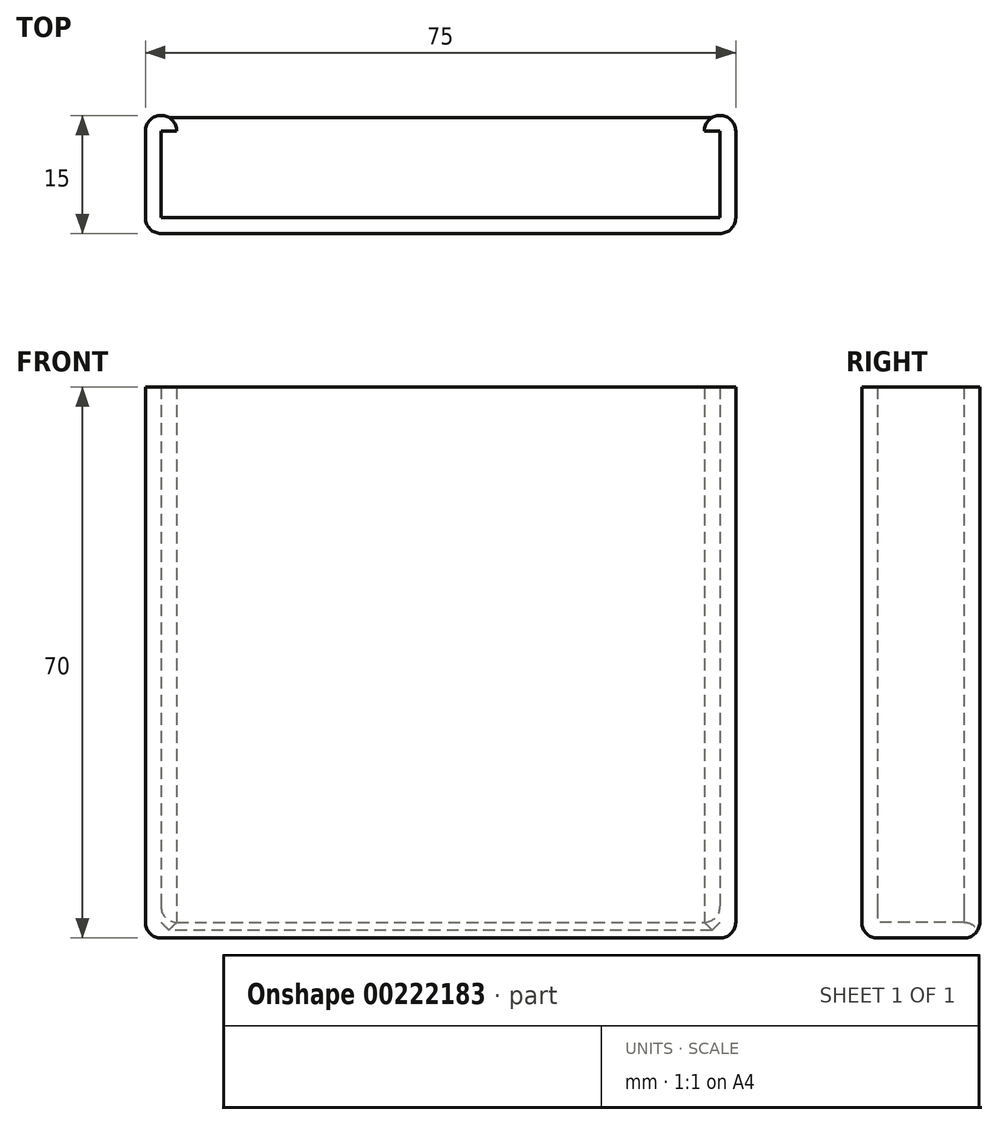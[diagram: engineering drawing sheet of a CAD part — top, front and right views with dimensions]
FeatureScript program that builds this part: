
annotation { "Feature Type Name" : "Feature", "Feature Type Description" : "" }
export const myFeature = defineFeature(function(context is Context, id is Id, definition is map)
    precondition{}
    {
        {
            var Q0;
            Q0=qCreatedBy(makeId("Top.planeOp"),FACE);
            var sketch = newSketch(context, id + "F3", { "sketchPlane" : qUnion([Q0])});
            skLineSegment(sketch, "E0", {"start": v(-37.5, 0) * mm, "end": v(37.5, 0) * mm});
            skLineSegment(sketch, "E1", {"start": v(37.5, 0) * mm, "end": v(37.5, 15) * mm});
            skLineSegment(sketch, "E2", {"start": v(37.5, 15) * mm, "end": v(33.5, 15) * mm});
            skLineSegment(sketch, "E3", {"start": v(33.5, 15) * mm, "end": v(33.5, 13) * mm});
            skLineSegment(sketch, "E4", {"start": v(33.5, 13) * mm, "end": v(35.5, 13) * mm});
            skLineSegment(sketch, "E5", {"start": v(35.5, 13) * mm, "end": v(35.5, 2) * mm});
            skLineSegment(sketch, "E6", {"start": v(35.5, 2) * mm, "end": v(-35.5, 2) * mm});
            skLineSegment(sketch, "E7", {"start": v(-35.5, 2) * mm, "end": v(-35.5, 13) * mm});
            skLineSegment(sketch, "E8", {"start": v(-35.5, 13) * mm, "end": v(-33.5, 13) * mm});
            skLineSegment(sketch, "E9", {"start": v(-33.5, 13) * mm, "end": v(-33.5, 15) * mm});
            skLineSegment(sketch, "E10", {"start": v(-33.5, 15) * mm, "end": v(-37.5, 15) * mm});
            skLineSegment(sketch, "E11", {"start": v(-37.5, 15) * mm, "end": v(-37.5, 0) * mm});
            skSolve(sketch);
        }
        {
            var Q0;
            Q0=qSketchRegion(id+"FxWtbJgkQHIbVw/JA_0",true);
            var Q1;
            Q1=makeQuery(id+"F3.imprint","IMPRINT",FACE,{"disambiguationData":[TD([[makeQuery(id+"F3.imprint","IMPRINT",EDGE,{"derivedFrom":sQuery(id+"F3.wireOp",EDGE,"E0")}),1.0]])]});
            extrude(context, id + "F0", {"entities" : qUnion([Q0, Q1]), "depth" : 70 * mm});
        }
        {
            var Q0;
            Q0=makeQuery(id+"F0.opExtrude","CAP_FACE",FACE,{"disambiguationData":[OSD([sQuery(id+"F3.wireOp",EDGE,"E0"),sQuery(id+"F3.wireOp",EDGE,"E1"),sQuery(id+"F3.wireOp",EDGE,"E2"),sQuery(id+"F3.wireOp",EDGE,"E3"),sQuery(id+"F3.wireOp",EDGE,"E4"),sQuery(id+"F3.wireOp",EDGE,"E5"),sQuery(id+"F3.wireOp",EDGE,"E6"),sQuery(id+"F3.wireOp",EDGE,"E7"),sQuery(id+"F3.wireOp",EDGE,"E8"),sQuery(id+"F3.wireOp",EDGE,"E9"),sQuery(id+"F3.wireOp",EDGE,"E10"),sQuery(id+"F3.wireOp",EDGE,"E11")])],"isStart":true});
            var sketch = newSketch(context, id + "F1", { "sketchPlane" : qUnion([Q0])});
            skLineSegment(sketch, "E12.bottom", {"start": v(37.5, -15) * mm, "end": v(-37.5, -15) * mm});
            skLineSegment(sketch, "E12.top", {"start": v(37.5, 0) * mm, "end": v(-37.5, 0) * mm});
            skLineSegment(sketch, "E12.left", {"start": v(37.5, -15) * mm, "end": v(37.5, 0) * mm});
            skLineSegment(sketch, "E12.right", {"start": v(-37.5, -15) * mm, "end": v(-37.5, 0) * mm});
            skSolve(sketch);
        }
        {
            var Q0;
            Q0=qSketchRegion(id+"F1",true);
            extrude(context, id + "F4", {"entities" : qUnion([Q0]), "operationType" : NewBodyOperationType.ADD, "oppositeDirection" : true, "depth" : 2 * mm});
        }
        {
            var Q0;
            Q0=makeQuery(id+"F0.opExtrude","CAP_EDGE",EDGE,{"disambiguationData":[OSD([sQuery(id+"F3.wireOp",EDGE,"E1")])],"isStart":true});
            var Q1;
            Q1=makeQuery(id+"F0.opExtrude","CAP_EDGE",EDGE,{"disambiguationData":[OSD([sQuery(id+"F3.wireOp",EDGE,"E11")])],"isStart":true});
            var Q2;
            Q2=makeQuery(id+"F4.boolean.opBoolean","INTERSECT",EDGE,{"derivedFrom":[makeQuery(id+"F0.opExtrude","SWEPT_FACE",FACE,{"disambiguationData":[OSD([sQuery(id+"F3.wireOp",EDGE,"E5")])]}),makeQuery(id+"F4.opExtrude","CAP_FACE",FACE,{"disambiguationData":[OSD([sQuery(id+"F1.wireOp",EDGE,"E12.bottom"),sQuery(id+"F1.wireOp",EDGE,"E12.top"),sQuery(id+"F1.wireOp",EDGE,"E12.left"),sQuery(id+"F1.wireOp",EDGE,"E12.right")])],"isStart":false})]});
            var Q3;
            Q3=makeQuery(id+"F4.boolean.opBoolean","INTERSECT",EDGE,{"derivedFrom":[makeQuery(id+"F0.opExtrude","SWEPT_FACE",FACE,{"disambiguationData":[OSD([sQuery(id+"F3.wireOp",EDGE,"E7")])]}),makeQuery(id+"F4.opExtrude","CAP_FACE",FACE,{"disambiguationData":[OSD([sQuery(id+"F1.wireOp",EDGE,"E12.bottom"),sQuery(id+"F1.wireOp",EDGE,"E12.top"),sQuery(id+"F1.wireOp",EDGE,"E12.left"),sQuery(id+"F1.wireOp",EDGE,"E12.right")])],"isStart":false})]});
            var Q4;
            Q4=makeQuery(id+"F0.opExtrude","SWEPT_EDGE",EDGE,{"disambiguationData":[OSD([sQuery(id+"F3.wireOp",EDGE,"E0"),sQuery(id+"F3.wireOp",EDGE,"E11")])]});
            var Q5;
            Q5=makeQuery(id+"F0.opExtrude","SWEPT_EDGE",EDGE,{"disambiguationData":[OSD([sQuery(id+"F3.wireOp",EDGE,"E0"),sQuery(id+"F3.wireOp",EDGE,"E1")])]});
            var Q6;
            Q6=makeQuery(id+"F0.opExtrude","SWEPT_EDGE",EDGE,{"disambiguationData":[OSD([sQuery(id+"F3.wireOp",EDGE,"E10"),sQuery(id+"F3.wireOp",EDGE,"E11")])]});
            var Q7;
            Q7=makeQuery(id+"F0.opExtrude","SWEPT_EDGE",EDGE,{"disambiguationData":[OSD([sQuery(id+"F3.wireOp",EDGE,"E1"),sQuery(id+"F3.wireOp",EDGE,"E2")])]});
            var Q8;
            Q8=makeQuery(id+"F0.opExtrude","SWEPT_EDGE",EDGE,{"disambiguationData":[OSD([sQuery(id+"F3.wireOp",EDGE,"E9"),sQuery(id+"F3.wireOp",EDGE,"E10")])]});
            var Q9;
            Q9=makeQuery(id+"F4.opExtrude","CAP_EDGE",EDGE,{"disambiguationData":[OSD([sQuery(id+"F1.wireOp",EDGE,"E12.bottom")])],"isStart":false});
            var Q10;
            Q10=makeQuery(id+"F0.opExtrude","SWEPT_EDGE",EDGE,{"disambiguationData":[OSD([sQuery(id+"F3.wireOp",EDGE,"E2"),sQuery(id+"F3.wireOp",EDGE,"E3")])]});
            var Q11;
            Q11=makeQuery(id+"F0.opExtrude","CAP_EDGE",EDGE,{"disambiguationData":[OSD([sQuery(id+"F3.wireOp",EDGE,"E0")])],"isStart":true});
            var Q12;
            Q12=makeQuery(id+"F4.boolean.opBoolean","MERGE",EDGE,{"derivedFrom":[makeQuery(id+"F0.opExtrude","CAP_EDGE",EDGE,{"disambiguationData":[OSD([sQuery(id+"F3.wireOp",EDGE,"E2")])],"isStart":true}),makeQuery(id+"F0.opExtrude","CAP_EDGE",EDGE,{"disambiguationData":[OSD([sQuery(id+"F3.wireOp",EDGE,"E10")])],"isStart":true}),makeQuery(id+"F4.opExtrude","CAP_EDGE",EDGE,{"disambiguationData":[OSD([sQuery(id+"F1.wireOp",EDGE,"E12.bottom")])],"isStart":true})]});
            fillet(context, id + "F2", {"entities" : qUnion([Q0, Q1, Q2, Q3, Q4, Q5, Q6, Q7, Q8, Q9, Q10, Q11, Q12]), "radius" : 2 * mm, "tangentPropagation" : true, "allowEdgeOverflow" : false});
        }
    });
